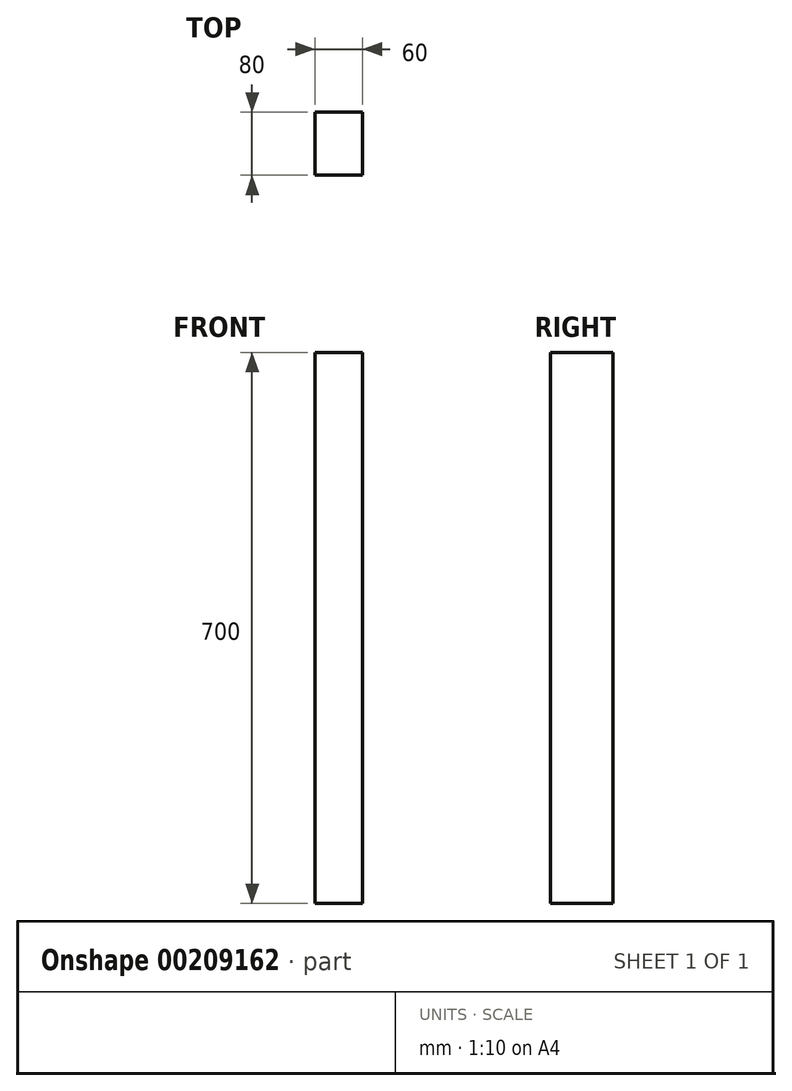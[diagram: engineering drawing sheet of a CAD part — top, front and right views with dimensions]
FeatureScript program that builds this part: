
annotation { "Feature Type Name" : "Feature", "Feature Type Description" : "" }
export const myFeature = defineFeature(function(context is Context, id is Id, definition is map)
    precondition{}
    {
        {
            var Q0;
            Q0=qCreatedBy(makeId("Front.planeOp"),FACE);
            var sketch = newSketch(context, id + "F0", { "sketchPlane" : qUnion([Q0])});
            skLineSegment(sketch, "E0.bottom", {"start": v(30, 350) * mm, "end": v(-30, 350) * mm});
            skLineSegment(sketch, "E0.top", {"start": v(30, -350) * mm, "end": v(-30, -350) * mm});
            skLineSegment(sketch, "E0.left", {"start": v(30, 350) * mm, "end": v(30, -350) * mm});
            skLineSegment(sketch, "E0.right", {"start": v(-30, 350) * mm, "end": v(-30, -350) * mm});
            skPoint(sketch, "E0.middle", {"position": v(0, 0) * mm});
            skSolve(sketch);
        }
        {
            var Q0;
            Q0=makeQuery(id+"F0.imprint","IMPRINT",FACE,{"disambiguationData":[TD([[makeQuery(id+"F0.imprint","IMPRINT",EDGE,{"derivedFrom":sQuery(id+"F0.wireOp",EDGE,"E0.bottom")}),1.0]])]});
            extrude(context, id + "F1", {"entities" : qUnion([Q0]), "depth" : 80 * mm, "offsetDistance" : 25 * mm});
        }
    });
